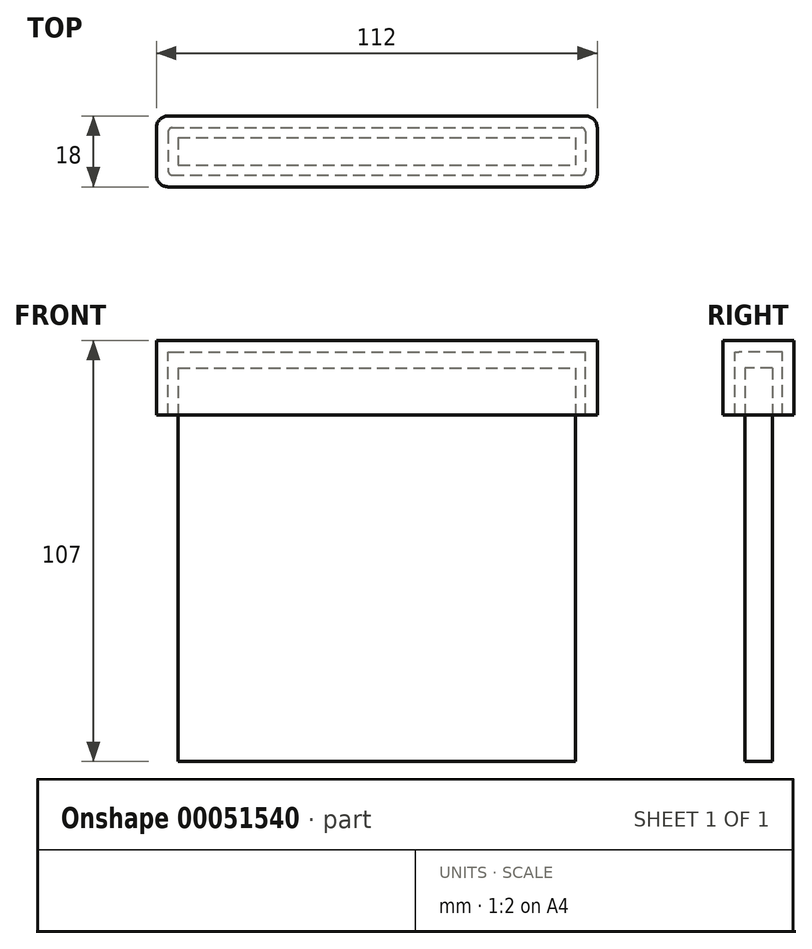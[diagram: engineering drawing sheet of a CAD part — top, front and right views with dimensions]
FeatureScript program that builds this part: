
annotation { "Feature Type Name" : "Feature", "Feature Type Description" : "" }
export const myFeature = defineFeature(function(context is Context, id is Id, definition is map)
    precondition{}
    {
        {
            var Q0;
            Q0=qCreatedBy(makeId("Top.planeOp"),FACE);
            var sketch = newSketch(context, id + "F0", { "sketchPlane" : qUnion([Q0])});
            skLineSegment(sketch, "E0.bottom", {"start": v(0, 0) * mm, "end": v(101, 0) * mm});
            skLineSegment(sketch, "E0.top", {"start": v(0, -7) * mm, "end": v(101, -7) * mm});
            skLineSegment(sketch, "E0.left", {"start": v(0, 0) * mm, "end": v(0, -7) * mm});
            skLineSegment(sketch, "E0.right", {"start": v(101, 0) * mm, "end": v(101, -7) * mm});
            skSolve(sketch);
        }
        {
            var Q0;
            Q0=makeQuery(id+"F0.imprint","IMPRINT",FACE,{"disambiguationData":[TD([[makeQuery(id+"F0.imprint","IMPRINT",EDGE,{"derivedFrom":sQuery(id+"F0.wireOp",EDGE,"E0.bottom")}),-1.0]])]});
            extrude(context, id + "F1", {"entities" : qUnion([Q0]), "depth" : 100 * mm});
        }
        {
            var Q0;
            Q0=makeQuery(id+"F1.opExtrude","CAP_FACE",FACE,{"disambiguationData":[OSD([sQuery(id+"F0.wireOp",EDGE,"E0.bottom"),sQuery(id+"F0.wireOp",EDGE,"E0.top"),sQuery(id+"F0.wireOp",EDGE,"E0.left"),sQuery(id+"F0.wireOp",EDGE,"E0.right")])],"isStart":false});
            var sketch = newSketch(context, id + "F2", { "sketchPlane" : qUnion([Q0])});
            skLineSegment(sketch, "E1.0", {"start": v(-2.5, 2.5) * mm, "end": v(103.5, 2.5) * mm});
            skLineSegment(sketch, "E1.1", {"start": v(-2.5, 2.5) * mm, "end": v(-2.5, -9.5) * mm});
            skLineSegment(sketch, "E1.2", {"start": v(-2.5, -9.5) * mm, "end": v(103.5, -9.5) * mm});
            skLineSegment(sketch, "E1.3", {"start": v(103.5, 2.5) * mm, "end": v(103.5, -9.5) * mm});
            skLineSegment(sketch, "E2.0", {"start": v(-5.5, 5.5) * mm, "end": v(106.5, 5.5) * mm});
            skLineSegment(sketch, "E2.1", {"start": v(-5.5, 5.5) * mm, "end": v(-5.5, -12.5) * mm});
            skLineSegment(sketch, "E2.2", {"start": v(-5.5, -12.5) * mm, "end": v(106.5, -12.5) * mm});
            skLineSegment(sketch, "E2.3", {"start": v(106.5, 5.5) * mm, "end": v(106.5, -12.5) * mm});
            skSolve(sketch);
        }
        {
            var Q0;
            Q0=makeQuery(id+"F2.imprint","IMPRINT",FACE,{"disambiguationData":[TD([[makeQuery(id+"F2.imprint","IMPRINT",EDGE,{"derivedFrom":sQuery(id+"F2.wireOp",EDGE,"E1.0")}),1.0]])]});
            extrude(context, id + "F3", {"entities" : qUnion([Q0]), "oppositeDirection" : true, "depth" : 12 * mm});
        }
        {
            var Q0;
            Q0=makeQuery(id+"F3.opExtrude","CAP_FACE",FACE,{"disambiguationData":[OSD([sQuery(id+"F2.wireOp",EDGE,"E1.0"),sQuery(id+"F2.wireOp",EDGE,"E1.1"),sQuery(id+"F2.wireOp",EDGE,"E1.2"),sQuery(id+"F2.wireOp",EDGE,"E1.3"),sQuery(id+"F2.wireOp",EDGE,"E2.0"),sQuery(id+"F2.wireOp",EDGE,"E2.1"),sQuery(id+"F2.wireOp",EDGE,"E2.2"),sQuery(id+"F2.wireOp",EDGE,"E2.3")])],"isStart":true});
            extrude(context, id + "F4", {"entities" : qUnion([Q0]), "operationType" : NewBodyOperationType.ADD, "depth" : 4 * mm});
        }
        {
            var Q0;
            Q0=makeQuery(id+"F4.opExtrude","CAP_FACE",FACE,{"disambiguationData":[OSD([sQuery(id+"F2.wireOp",EDGE,"E1.0"),sQuery(id+"F2.wireOp",EDGE,"E1.1"),sQuery(id+"F2.wireOp",EDGE,"E1.2"),sQuery(id+"F2.wireOp",EDGE,"E1.3"),sQuery(id+"F2.wireOp",EDGE,"E2.0"),sQuery(id+"F2.wireOp",EDGE,"E2.1"),sQuery(id+"F2.wireOp",EDGE,"E2.2"),sQuery(id+"F2.wireOp",EDGE,"E2.3")])],"isStart":false});
            var sketch = newSketch(context, id + "F5", { "sketchPlane" : qUnion([Q0])});
            skLineSegment(sketch, "E3.bottom", {"start": v(-5.5, 5.5) * mm, "end": v(106.5, 5.5) * mm});
            skLineSegment(sketch, "E3.top", {"start": v(-5.5, -12.5) * mm, "end": v(106.5, -12.5) * mm});
            skLineSegment(sketch, "E3.left", {"start": v(-5.5, 5.5) * mm, "end": v(-5.5, -12.5) * mm});
            skLineSegment(sketch, "E3.right", {"start": v(106.5, 5.5) * mm, "end": v(106.5, -12.5) * mm});
            skSolve(sketch);
        }
        {
            var Q0;
            {var subQ0=sQuery(id+"F2.wireOp",EDGE,"E2.2");var subQ1=sQuery(id+"F2.wireOp",EDGE,"E2.1");Q0=makeQuery(id+"F4.boolean.opBoolean","MERGE",EDGE,{"derivedFrom":[makeQuery(id+"F3.opExtrude","SWEPT_EDGE",EDGE,{"disambiguationData":[OSD([subQ1,subQ0])]}),makeQuery(id+"F4.opExtrude","SWEPT_EDGE",EDGE,{"disambiguationData":[OSD([subQ1,subQ0])]})]});}
            var Q1;
            {var subQ0=sQuery(id+"F2.wireOp",EDGE,"E2.1");var subQ1=sQuery(id+"F2.wireOp",EDGE,"E2.0");Q1=makeQuery(id+"F4.boolean.opBoolean","MERGE",EDGE,{"derivedFrom":[makeQuery(id+"F3.opExtrude","SWEPT_EDGE",EDGE,{"disambiguationData":[OSD([subQ1,subQ0])]}),makeQuery(id+"F4.opExtrude","SWEPT_EDGE",EDGE,{"disambiguationData":[OSD([subQ1,subQ0])]})]});}
            var Q2;
            {var subQ0=sQuery(id+"F2.wireOp",EDGE,"E2.3");var subQ1=sQuery(id+"F2.wireOp",EDGE,"E2.0");Q2=makeQuery(id+"F4.boolean.opBoolean","MERGE",EDGE,{"derivedFrom":[makeQuery(id+"F3.opExtrude","SWEPT_EDGE",EDGE,{"disambiguationData":[OSD([subQ1,subQ0])]}),makeQuery(id+"F4.opExtrude","SWEPT_EDGE",EDGE,{"disambiguationData":[OSD([subQ1,subQ0])]})]});}
            var Q3;
            {var subQ0=sQuery(id+"F2.wireOp",EDGE,"E2.3");var subQ1=sQuery(id+"F2.wireOp",EDGE,"E2.2");Q3=makeQuery(id+"F4.boolean.opBoolean","MERGE",EDGE,{"derivedFrom":[makeQuery(id+"F3.opExtrude","SWEPT_EDGE",EDGE,{"disambiguationData":[OSD([subQ1,subQ0])]}),makeQuery(id+"F4.opExtrude","SWEPT_EDGE",EDGE,{"disambiguationData":[OSD([subQ1,subQ0])]})]});}
            fillet(context, id + "F6", {"entities" : qUnion([Q0, Q1, Q2, Q3]), "radius" : 3 * mm, "tangentPropagation" : true, "allowEdgeOverflow" : false});
        }
        {
            var Q0;
            Q0 = qSketchRegion(id + "F5", true);
            extrude(context, id + "F7", {"entities" : qUnion([Q0]), "operationType" : NewBodyOperationType.ADD, "depth" : 3 * mm});
        }
        {
            var Q0;
            Q0=makeQuery(id+"F7.opExtrude","SWEPT_EDGE",EDGE,{"disambiguationData":[OSD([sQuery(id+"F5.wireOp",EDGE,"E3.top"),sQuery(id+"F5.wireOp",EDGE,"E3.right")])]});
            var Q1;
            Q1=makeQuery(id+"F7.opExtrude","SWEPT_EDGE",EDGE,{"disambiguationData":[OSD([sQuery(id+"F5.wireOp",EDGE,"E3.bottom"),sQuery(id+"F5.wireOp",EDGE,"E3.right")])]});
            var Q2;
            Q2=makeQuery(id+"F7.opExtrude","SWEPT_EDGE",EDGE,{"disambiguationData":[OSD([sQuery(id+"F5.wireOp",EDGE,"E3.bottom"),sQuery(id+"F5.wireOp",EDGE,"E3.left")])]});
            var Q3;
            Q3=makeQuery(id+"F7.opExtrude","SWEPT_EDGE",EDGE,{"disambiguationData":[OSD([sQuery(id+"F5.wireOp",EDGE,"E3.top"),sQuery(id+"F5.wireOp",EDGE,"E3.left")])]});
            fillet(context, id + "F8", {"entities" : qUnion([Q0, Q1, Q2, Q3]), "radius" : 3 * mm, "tangentPropagation" : true, "allowEdgeOverflow" : false});
        }
        {
            var Q0;
            Q0=makeQuery(id+"F4.opExtrude","CAP_EDGE",EDGE,{"disambiguationData":[OSD([sQuery(id+"F2.wireOp",EDGE,"E1.1")])],"isStart":false});
            var Q1;
            {var subQ0=sQuery(id+"F2.wireOp",EDGE,"E1.2");var subQ1=sQuery(id+"F2.wireOp",EDGE,"E1.1");Q1=makeQuery(id+"F4.boolean.opBoolean","MERGE",EDGE,{"derivedFrom":[makeQuery(id+"F3.opExtrude","SWEPT_EDGE",EDGE,{"disambiguationData":[OSD([subQ1,subQ0])]}),makeQuery(id+"F4.opExtrude","SWEPT_EDGE",EDGE,{"disambiguationData":[OSD([subQ1,subQ0])]})]});}
            var Q2;
            Q2=makeQuery(id+"F4.opExtrude","CAP_EDGE",EDGE,{"disambiguationData":[OSD([sQuery(id+"F2.wireOp",EDGE,"E1.2")])],"isStart":false});
            var Q3;
            Q3=makeQuery(id+"F4.opExtrude","CAP_EDGE",EDGE,{"disambiguationData":[OSD([sQuery(id+"F2.wireOp",EDGE,"E1.0")])],"isStart":false});
            var Q4;
            {var subQ0=sQuery(id+"F2.wireOp",EDGE,"E1.1");var subQ1=sQuery(id+"F2.wireOp",EDGE,"E1.0");Q4=makeQuery(id+"F4.boolean.opBoolean","MERGE",EDGE,{"derivedFrom":[makeQuery(id+"F3.opExtrude","SWEPT_EDGE",EDGE,{"disambiguationData":[OSD([subQ1,subQ0])]}),makeQuery(id+"F4.opExtrude","SWEPT_EDGE",EDGE,{"disambiguationData":[OSD([subQ1,subQ0])]})]});}
            var Q5;
            {var subQ0=sQuery(id+"F2.wireOp",EDGE,"E1.3");var subQ1=sQuery(id+"F2.wireOp",EDGE,"E1.0");Q5=makeQuery(id+"F4.boolean.opBoolean","MERGE",EDGE,{"derivedFrom":[makeQuery(id+"F3.opExtrude","SWEPT_EDGE",EDGE,{"disambiguationData":[OSD([subQ1,subQ0])]}),makeQuery(id+"F4.opExtrude","SWEPT_EDGE",EDGE,{"disambiguationData":[OSD([subQ1,subQ0])]})]});}
            var Q6;
            Q6=makeQuery(id+"F4.opExtrude","CAP_EDGE",EDGE,{"disambiguationData":[OSD([sQuery(id+"F2.wireOp",EDGE,"E1.3")])],"isStart":false});
            var Q7;
            {var subQ0=sQuery(id+"F2.wireOp",EDGE,"E1.3");var subQ1=sQuery(id+"F2.wireOp",EDGE,"E1.2");Q7=makeQuery(id+"F4.boolean.opBoolean","MERGE",EDGE,{"derivedFrom":[makeQuery(id+"F3.opExtrude","SWEPT_EDGE",EDGE,{"disambiguationData":[OSD([subQ1,subQ0])]}),makeQuery(id+"F4.opExtrude","SWEPT_EDGE",EDGE,{"disambiguationData":[OSD([subQ1,subQ0])]})]});}
            fillet(context, id + "F9", {"entities" : qUnion([Q0, Q1, Q2, Q3, Q4, Q5, Q6, Q7]), "radius" : 1 * mm, "tangentPropagation" : true, "allowEdgeOverflow" : false});
        }
    });
